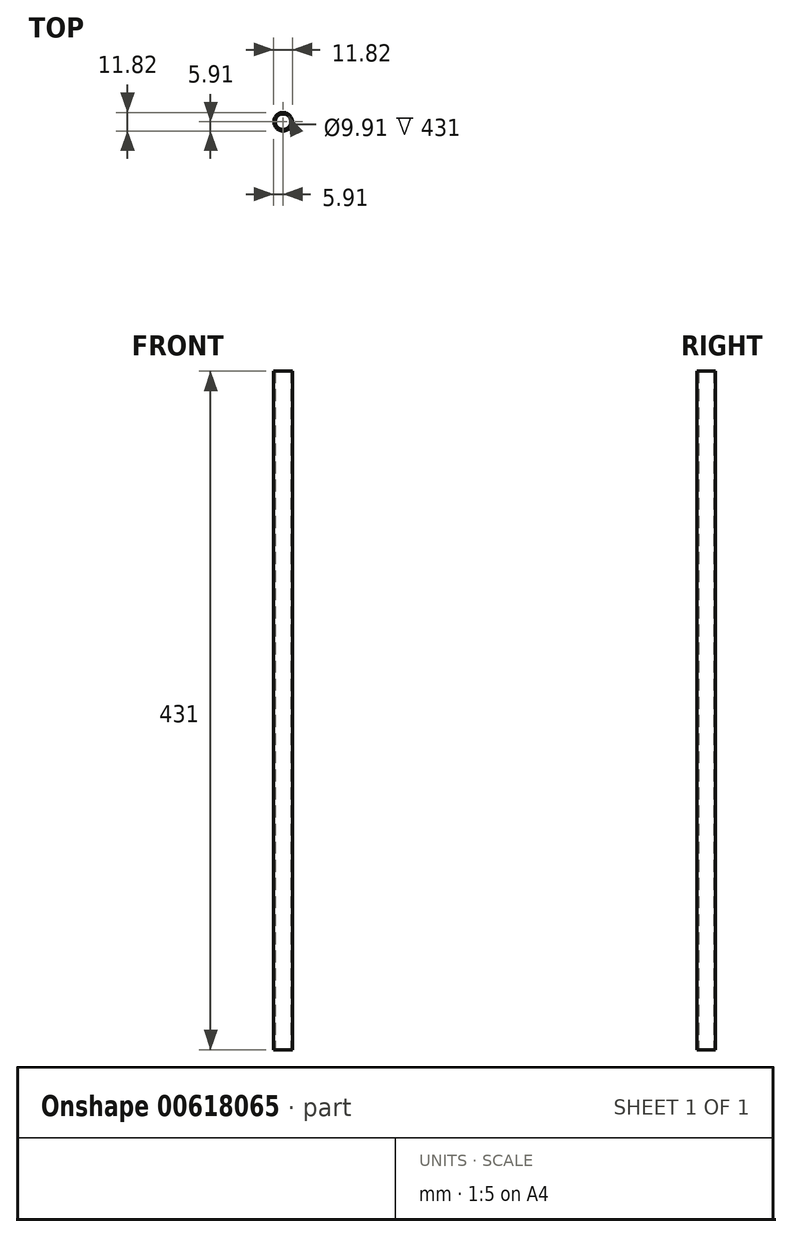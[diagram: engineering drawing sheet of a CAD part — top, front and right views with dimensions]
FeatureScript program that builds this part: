
annotation { "Feature Type Name" : "Feature", "Feature Type Description" : "" }
export const myFeature = defineFeature(function(context is Context, id is Id, definition is map)
    precondition{}
    {
        {
            var Q0;
            Q0=qCreatedBy(makeId("Top.planeOp"),FACE);
            var sketch = newSketch(context, id + "F0", { "sketchPlane" : qUnion([Q0])});
            skCircle(sketch, "E0", {"center": v(0, 0) * mm, "radius": 5.9 * mm});
            skCircle(sketch, "E1", {"center": v(0, 0) * mm, "radius": 4.95 * mm});
            skSolve(sketch);
        }
        {
            var Q0;
            Q0=makeQuery(id+"F0.imprint","IMPRINT",FACE,{"disambiguationData":[TD([[makeQuery(id+"F0.imprint","IMPRINT",EDGE,{"derivedFrom":sQuery(id+"F0.wireOp",EDGE,"E0")}),1.0]])]});
            extrude(context, id + "F1", {"entities" : qUnion([Q0]), "endBound" : BoundingType.SYMMETRIC, "depth" : 431 * mm, "offsetDistance" : 25.4 * mm});
        }
    });
